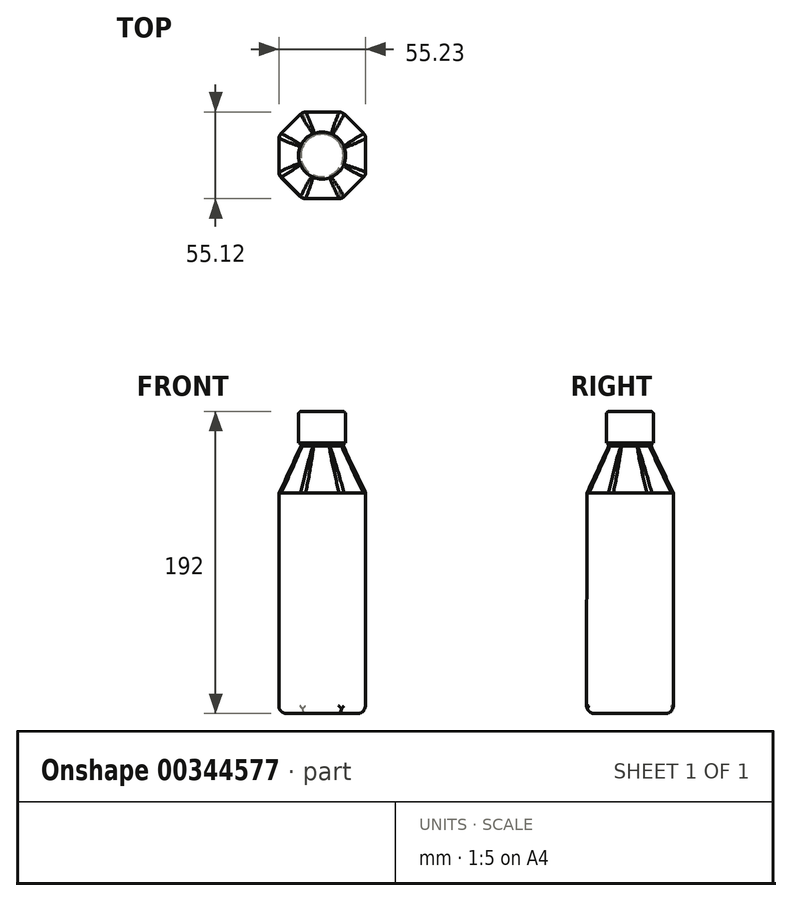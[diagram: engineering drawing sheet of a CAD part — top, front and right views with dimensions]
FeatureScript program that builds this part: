
annotation { "Feature Type Name" : "Feature", "Feature Type Description" : "" }
export const myFeature = defineFeature(function(context is Context, id is Id, definition is map)
    precondition{}
    {
        {
            var Q0;
            Q0=qCreatedBy(makeId("Top.planeOp"),FACE);
            cPlane(context, id + "F0", {"entities" : qUnion([Q0]), "cplaneType" : CPlaneType.OFFSET, "offset" : 140 * mm, "width" : 150 * mm, "height" : 150 * mm});
        }
        {
            var Q0;
            Q0=qCreatedBy(makeId("Top.planeOp"),FACE);
            var sketch = newSketch(context, id + "F1", { "sketchPlane" : qUnion([Q0])});
            skLineSegment(sketch, "E0.bottom", {"start": v(27.5, 27.5) * mm, "end": v(-27.5, 27.5) * mm});
            skLineSegment(sketch, "E0.top", {"start": v(27.5, -27.5) * mm, "end": v(-27.5, -27.5) * mm});
            skLineSegment(sketch, "E0.left", {"start": v(27.5, 27.5) * mm, "end": v(27.5, -27.5) * mm});
            skLineSegment(sketch, "E0.right", {"start": v(-27.5, 27.5) * mm, "end": v(-27.5, -27.5) * mm});
            skPoint(sketch, "E0.middle", {"position": v(0, 0) * mm});
            skSolve(sketch);
        }
        {
            var Q0;
            Q0=qCreatedBy(id+"F0.planeOp",FACE);
            var sketch = newSketch(context, id + "F2", { "sketchPlane" : qUnion([Q0])});
            skLineSegment(sketch, "E1.bottom", {"start": v(27.74, 27.62) * mm, "end": v(-27.26, 27.62) * mm});
            skLineSegment(sketch, "E1.top", {"start": v(27.74, -27.38) * mm, "end": v(-27.26, -27.38) * mm});
            skLineSegment(sketch, "E1.left", {"start": v(27.74, 27.62) * mm, "end": v(27.74, -27.38) * mm});
            skLineSegment(sketch, "E1.right", {"start": v(-27.26, 27.62) * mm, "end": v(-27.26, -27.38) * mm});
            skPoint(sketch, "E1.middle", {"position": v(0.24, 0.12) * mm});
            skSolve(sketch);
        }
        {
            var Q0;
            Q0=makeQuery(id+"F1.imprint","IMPRINT",FACE,{"disambiguationData":[TD([[makeQuery(id+"F1.imprint","IMPRINT",EDGE,{"derivedFrom":sQuery(id+"F1.wireOp",EDGE,"E0.bottom")}),1.0]])]});
            var Q1;
            Q1=makeQuery(id+"F2.imprint","IMPRINT",FACE,{"disambiguationData":[TD([[makeQuery(id+"F2.imprint","IMPRINT",EDGE,{"derivedFrom":sQuery(id+"F2.wireOp",EDGE,"E1.bottom")}),1.0]])]});
            loft(context, id + "F3", {"sheetProfilesArray" : [{ "sheetProfileEntities" : qUnion([Q0]) }, { "sheetProfileEntities" : qUnion([Q1]) }]});
        }
        {
            var Q0;
            Q0=makeQuery(id+"F3.opLoft","SWEPT_EDGE",EDGE,{"disambiguationData":[OSD([sQuery(id+"F1.wireOp",EDGE,"E0.top"),sQuery(id+"F1.wireOp",EDGE,"E0.left"),sQuery(id+"F2.wireOp",EDGE,"E1.top"),sQuery(id+"F2.wireOp",EDGE,"E1.left")])]});
            var Q1;
            Q1=makeQuery(id+"F3.opLoft","SWEPT_EDGE",EDGE,{"disambiguationData":[OSD([sQuery(id+"F1.wireOp",EDGE,"E0.bottom"),sQuery(id+"F1.wireOp",EDGE,"E0.left"),sQuery(id+"F2.wireOp",EDGE,"E1.bottom"),sQuery(id+"F2.wireOp",EDGE,"E1.left")])]});
            var Q2;
            Q2=makeQuery(id+"F3.opLoft","SWEPT_EDGE",EDGE,{"disambiguationData":[OSD([sQuery(id+"F1.wireOp",EDGE,"E0.top"),sQuery(id+"F1.wireOp",EDGE,"E0.right"),sQuery(id+"F2.wireOp",EDGE,"E1.top"),sQuery(id+"F2.wireOp",EDGE,"E1.right")])]});
            var Q3;
            Q3=makeQuery(id+"F3.opLoft","SWEPT_EDGE",EDGE,{"disambiguationData":[OSD([sQuery(id+"F1.wireOp",EDGE,"E0.bottom"),sQuery(id+"F1.wireOp",EDGE,"E0.right"),sQuery(id+"F2.wireOp",EDGE,"E1.bottom"),sQuery(id+"F2.wireOp",EDGE,"E1.right")])]});
            chamfer(context, id + "F4", {"entities" : qUnion([Q0, Q1, Q2, Q3]), "width" : 15 * mm, "tangentPropagation" : true});
        }
        {
            var Q0;
            Q0=qCreatedBy(id+"F0.planeOp",FACE);
            cPlane(context, id + "F5", {"entities" : qUnion([Q0]), "cplaneType" : CPlaneType.OFFSET, "offset" : 30 * mm, "width" : 150 * mm, "height" : 150 * mm});
        }
        {
            var Q0;
            Q0=qCreatedBy(id+"F5.planeOp",FACE);
            var sketch = newSketch(context, id + "F6", { "sketchPlane" : qUnion([Q0])});
            skCircle(sketch, "E2", {"center": v(0, 0) * mm, "radius": 13.5 * mm});
            skSolve(sketch);
        }
        {
            var Q1;
            Q1=makeQuery(id+"F3.opLoft","CAP_FACE",FACE,{"disambiguationData":[OSD([makeQuery(id+"F2.imprint","IMPRINT",FACE,{"disambiguationData":[TD([[makeQuery(id+"F2.imprint","IMPRINT",EDGE,{"derivedFrom":sQuery(id+"F2.wireOp",EDGE,"E1.bottom")}),1.0]])]})])],"isStart":true});
            var Q2;
            Q2=makeQuery(id+"F6.imprint","IMPRINT",FACE,{"disambiguationData":[TD([[makeQuery(id+"F6.imprint","IMPRINT",EDGE,{"derivedFrom":sQuery(id+"F6.wireOp",EDGE,"E2")}),1.0]])]});
            loft(context, id + "F7", {"operationType" : NewBodyOperationType.ADD, "sheetProfilesArray" : [{ "sheetProfileEntities" : qUnion([Q1]) }, { "sheetProfileEntities" : qUnion([Q2]) }]});
        }
        {
            var Q0;
            {var subQ0=sQuery(id+"F1.wireOp",EDGE,"E0.bottom");var subQ1=sQuery(id+"F1.wireOp",EDGE,"E0.left");Q0=makeQuery(id+"F4.opChamfer","BLEND_EDGE",EDGE,{"blendedFrom":[makeQuery(id+"F3.opLoft","SWEPT_EDGE",EDGE,{"disambiguationData":[OSD([subQ0,subQ1,sQuery(id+"F2.wireOp",EDGE,"E1.bottom"),sQuery(id+"F2.wireOp",EDGE,"E1.left")])]}),makeQuery(id+"F3.opLoft","CAP_FACE",FACE,{"disambiguationData":[OSD([makeQuery(id+"F1.imprint","IMPRINT",FACE,{"disambiguationData":[TD([[makeQuery(id+"F1.imprint","IMPRINT",EDGE,{"derivedFrom":subQ0}),1.0]])]})])],"isStart":true})],"blendedInto":[makeQuery(id+"F3.opLoft","CAP_FACE",FACE,{"disambiguationData":[OSD([makeQuery(id+"F1.imprint","IMPRINT",FACE,{"disambiguationData":[TD([[makeQuery(id+"F1.imprint","IMPRINT",EDGE,{"derivedFrom":subQ0}),1.0]])]})])],"isStart":true})]});}
            var Q1;
            Q1=makeQuery(id+"F3.opLoft","MID_CAP_EDGE",EDGE,{"disambiguationData":[OSD([sQuery(id+"F1.wireOp",EDGE,"E0.bottom"),sQuery(id+"F1.wireOp",EDGE,"E0.top"),sQuery(id+"F1.wireOp",EDGE,"E0.left")])],"capPos":0.0});
            var Q2;
            {var subQ0=sQuery(id+"F1.wireOp",EDGE,"E0.top");var subQ1=sQuery(id+"F1.wireOp",EDGE,"E0.left");Q2=makeQuery(id+"F4.opChamfer","BLEND_EDGE",EDGE,{"blendedFrom":[makeQuery(id+"F3.opLoft","SWEPT_EDGE",EDGE,{"disambiguationData":[OSD([subQ0,subQ1,sQuery(id+"F2.wireOp",EDGE,"E1.top"),sQuery(id+"F2.wireOp",EDGE,"E1.left")])]}),makeQuery(id+"F3.opLoft","CAP_FACE",FACE,{"disambiguationData":[OSD([makeQuery(id+"F1.imprint","IMPRINT",FACE,{"disambiguationData":[TD([[makeQuery(id+"F1.imprint","IMPRINT",EDGE,{"derivedFrom":sQuery(id+"F1.wireOp",EDGE,"E0.bottom")}),1.0]])]})])],"isStart":true})],"blendedInto":[makeQuery(id+"F3.opLoft","CAP_FACE",FACE,{"disambiguationData":[OSD([makeQuery(id+"F1.imprint","IMPRINT",FACE,{"disambiguationData":[TD([[makeQuery(id+"F1.imprint","IMPRINT",EDGE,{"derivedFrom":sQuery(id+"F1.wireOp",EDGE,"E0.bottom")}),1.0]])]})])],"isStart":true})]});}
            var Q3;
            Q3=makeQuery(id+"F3.opLoft","MID_CAP_EDGE",EDGE,{"disambiguationData":[OSD([sQuery(id+"F1.wireOp",EDGE,"E0.bottom"),sQuery(id+"F1.wireOp",EDGE,"E0.left"),sQuery(id+"F1.wireOp",EDGE,"E0.right")])],"capPos":0.0});
            var Q4;
            {var subQ0=sQuery(id+"F1.wireOp",EDGE,"E0.bottom");var subQ1=sQuery(id+"F1.wireOp",EDGE,"E0.right");Q4=makeQuery(id+"F4.opChamfer","BLEND_EDGE",EDGE,{"blendedFrom":[makeQuery(id+"F3.opLoft","SWEPT_EDGE",EDGE,{"disambiguationData":[OSD([subQ0,subQ1,sQuery(id+"F2.wireOp",EDGE,"E1.bottom"),sQuery(id+"F2.wireOp",EDGE,"E1.right")])]}),makeQuery(id+"F3.opLoft","CAP_FACE",FACE,{"disambiguationData":[OSD([makeQuery(id+"F1.imprint","IMPRINT",FACE,{"disambiguationData":[TD([[makeQuery(id+"F1.imprint","IMPRINT",EDGE,{"derivedFrom":subQ0}),1.0]])]})])],"isStart":true})],"blendedInto":[makeQuery(id+"F3.opLoft","CAP_FACE",FACE,{"disambiguationData":[OSD([makeQuery(id+"F1.imprint","IMPRINT",FACE,{"disambiguationData":[TD([[makeQuery(id+"F1.imprint","IMPRINT",EDGE,{"derivedFrom":subQ0}),1.0]])]})])],"isStart":true})]});}
            var Q5;
            Q5=makeQuery(id+"F3.opLoft","MID_CAP_EDGE",EDGE,{"disambiguationData":[OSD([sQuery(id+"F1.wireOp",EDGE,"E0.bottom"),sQuery(id+"F1.wireOp",EDGE,"E0.top"),sQuery(id+"F1.wireOp",EDGE,"E0.right")])],"capPos":0.0});
            var Q6;
            {var subQ0=sQuery(id+"F1.wireOp",EDGE,"E0.top");var subQ1=sQuery(id+"F1.wireOp",EDGE,"E0.right");Q6=makeQuery(id+"F4.opChamfer","BLEND_EDGE",EDGE,{"blendedFrom":[makeQuery(id+"F3.opLoft","SWEPT_EDGE",EDGE,{"disambiguationData":[OSD([subQ0,subQ1,sQuery(id+"F2.wireOp",EDGE,"E1.top"),sQuery(id+"F2.wireOp",EDGE,"E1.right")])]}),makeQuery(id+"F3.opLoft","CAP_FACE",FACE,{"disambiguationData":[OSD([makeQuery(id+"F1.imprint","IMPRINT",FACE,{"disambiguationData":[TD([[makeQuery(id+"F1.imprint","IMPRINT",EDGE,{"derivedFrom":sQuery(id+"F1.wireOp",EDGE,"E0.bottom")}),1.0]])]})])],"isStart":true})],"blendedInto":[makeQuery(id+"F3.opLoft","CAP_FACE",FACE,{"disambiguationData":[OSD([makeQuery(id+"F1.imprint","IMPRINT",FACE,{"disambiguationData":[TD([[makeQuery(id+"F1.imprint","IMPRINT",EDGE,{"derivedFrom":sQuery(id+"F1.wireOp",EDGE,"E0.bottom")}),1.0]])]})])],"isStart":true})]});}
            var Q7;
            Q7=makeQuery(id+"F3.opLoft","MID_CAP_EDGE",EDGE,{"disambiguationData":[OSD([sQuery(id+"F1.wireOp",EDGE,"E0.top"),sQuery(id+"F1.wireOp",EDGE,"E0.left"),sQuery(id+"F1.wireOp",EDGE,"E0.right")])],"capPos":0.0});
            fillet(context, id + "F8", {"entities" : qUnion([Q0, Q1, Q2, Q3, Q4, Q5, Q6, Q7]), "radius" : 5 * mm, "tangentPropagation" : true, "allowEdgeOverflow" : false});
        }
        {
            var Q0;
            Q0=qCreatedBy(id+"F5.planeOp",FACE);
            cPlane(context, id + "F9", {"entities" : qUnion([Q0]), "cplaneType" : CPlaneType.OFFSET, "offset" : 2 * mm, "width" : 150 * mm, "height" : 150 * mm});
        }
        {
            var Q0;
            Q0=qCreatedBy(id+"F9.planeOp",FACE);
            var sketch = newSketch(context, id + "F10", { "sketchPlane" : qUnion([Q0])});
            skCircle(sketch, "E3", {"center": v(0, 0) * mm, "radius": 13.5 * mm});
            skSolve(sketch);
        }
        {
            var Q0;
            Q0=makeQuery(id+"F6.imprint","IMPRINT",FACE,{"disambiguationData":[TD([[makeQuery(id+"F6.imprint","IMPRINT",EDGE,{"derivedFrom":sQuery(id+"F6.wireOp",EDGE,"E2")}),1.0]])]});
            var Q1;
            Q1=makeQuery(id+"F10.imprint","IMPRINT",FACE,{"disambiguationData":[TD([[makeQuery(id+"F10.imprint","IMPRINT",EDGE,{"derivedFrom":sQuery(id+"F10.wireOp",EDGE,"E3")}),1.0]])]});
            loft(context, id + "F11", {"sheetProfilesArray" : [{ "sheetProfileEntities" : qUnion([Q0]) }, { "sheetProfileEntities" : qUnion([Q1]) }]});
        }
        {
            var Q0;
            Q0=qCreatedBy(id+"F9.planeOp",FACE);
            var sketch = newSketch(context, id + "F12", { "sketchPlane" : qUnion([Q0])});
            skCircle(sketch, "E4", {"center": v(0, 0) * mm, "radius": 15 * mm});
            skSolve(sketch);
        }
        {
            var Q0;
            Q0=qCreatedBy(id+"F9.planeOp",FACE);
            cPlane(context, id + "F13", {"entities" : qUnion([Q0]), "cplaneType" : CPlaneType.OFFSET, "offset" : 20 * mm, "width" : 150 * mm, "height" : 150 * mm});
        }
        {
            var Q0;
            Q0=qCreatedBy(id+"F13.planeOp",FACE);
            var sketch = newSketch(context, id + "F14", { "sketchPlane" : qUnion([Q0])});
            skCircle(sketch, "E5", {"center": v(0, 0) * mm, "radius": 15 * mm});
            skSolve(sketch);
        }
        {
            var Q1;
            Q1=makeQuery(id+"F14.imprint","IMPRINT",FACE,{"disambiguationData":[TD([[makeQuery(id+"F14.imprint","IMPRINT",EDGE,{"derivedFrom":sQuery(id+"F14.wireOp",EDGE,"E5")}),1.0]])]});
            var Q2;
            Q2=makeQuery(id+"F12.imprint","IMPRINT",FACE,{"disambiguationData":[TD([[makeQuery(id+"F12.imprint","IMPRINT",EDGE,{"derivedFrom":sQuery(id+"F12.wireOp",EDGE,"E4")}),1.0]])]});
            loft(context, id + "F15", {"operationType" : NewBodyOperationType.ADD, "sheetProfilesArray" : [{ "sheetProfileEntities" : qUnion([Q1]) }, { "sheetProfileEntities" : qUnion([Q2]) }]});
        }
        {
            var Q0;
            Q0=makeQuery(id+"F15.opLoft","MID_CAP_EDGE",EDGE,{"disambiguationData":[OSD([sQuery(id+"F14.wireOp",EDGE,"E5")])],"capPos":0.0});
            fillet(context, id + "F16", {"entities" : qUnion([Q0]), "radius" : 2 * mm, "tangentPropagation" : true, "allowEdgeOverflow" : false});
        }
        {
            var Q0;
            {var subQ0=sQuery(id+"F6.wireOp",EDGE,"E2");var subQ1=sQuery(id+"F2.wireOp",EDGE,"E1.bottom");var subQ2=sQuery(id+"F2.wireOp",EDGE,"E1.top");var subQ3=sQuery(id+"F2.wireOp",EDGE,"E1.left");var subQ4=sQuery(id+"F2.wireOp",EDGE,"E1.right");var subQ5=makeQuery(id+"F2.imprint","IMPRINT",FACE,{"disambiguationData":[TD([[makeQuery(id+"F2.imprint","IMPRINT",EDGE,{"derivedFrom":subQ1}),1.0]])]});var subQ6=makeQuery(id+"F3.opLoft","CAP_FACE",FACE,{"disambiguationData":[OSD([subQ5])],"isStart":true});var subQ7=sQuery(id+"F1.wireOp",EDGE,"E0.right");var subQ8=sQuery(id+"F1.wireOp",EDGE,"E0.left");var subQ9=sQuery(id+"F1.wireOp",EDGE,"E0.top");var subQ10=makeQuery(id+"F3.opLoft","SWEPT_EDGE",EDGE,{"disambiguationData":[OSD([subQ9,subQ8,subQ2,subQ3])]});var subQ11=sQuery(id+"F1.wireOp",EDGE,"E0.bottom");Q0=makeQuery(id+"F7.opLoft","SWEPT_EDGE",EDGE,{"disambiguationData":[OSD([subQ11,subQ9,subQ8,subQ7,subQ1,subQ2,subQ3,subQ4,subQ5,subQ0]),TDD([makeQuery(id+"F4.opChamfer","BLEND_VERTEX",VERTEX,{"blendedFrom":[subQ10,makeQuery(id+"F3.opLoft","SWEPT_FACE",FACE,{"disambiguationData":[OSD([subQ11,subQ9,subQ8,subQ1,subQ2,subQ3])]}),subQ6],"blendedInto":[makeQuery(id+"F3.opLoft","SWEPT_FACE",FACE,{"disambiguationData":[OSD([subQ11,subQ9,subQ8,subQ1,subQ2,subQ3])]}),subQ6]}),makeQuery(id+"F4.opChamfer","BLEND_VERTEX",VERTEX,{"blendedFrom":[subQ10,makeQuery(id+"F3.opLoft","SWEPT_FACE",FACE,{"disambiguationData":[OSD([subQ9,subQ8,subQ7,subQ2,subQ3,subQ4])]}),subQ6],"blendedInto":[makeQuery(id+"F3.opLoft","SWEPT_FACE",FACE,{"disambiguationData":[OSD([subQ9,subQ8,subQ7,subQ2,subQ3,subQ4])]}),subQ6]}),makeQuery(id+"F6.imprint","IMPRINT",EDGE,{"derivedFrom":subQ0})])]});}
            var Q1;
            {var subQ0=sQuery(id+"F2.wireOp",EDGE,"E1.bottom");var subQ1=sQuery(id+"F2.wireOp",EDGE,"E1.top");var subQ2=sQuery(id+"F2.wireOp",EDGE,"E1.left");Q1=makeQuery(id+"F7.opLoft","SWEPT_EDGE",EDGE,{"disambiguationData":[OSD([sQuery(id+"F1.wireOp",EDGE,"E0.bottom"),sQuery(id+"F1.wireOp",EDGE,"E0.top"),sQuery(id+"F1.wireOp",EDGE,"E0.left"),subQ0,subQ1,subQ2,makeQuery(id+"F2.imprint","IMPRINT",FACE,{"disambiguationData":[TD([[makeQuery(id+"F2.imprint","IMPRINT",EDGE,{"derivedFrom":subQ0}),1.0]])]}),sQuery(id+"F6.wireOp",EDGE,"E2")])]});}
            var Q2;
            {var subQ0=sQuery(id+"F2.wireOp",EDGE,"E1.bottom");var subQ1=sQuery(id+"F2.wireOp",EDGE,"E1.left");var subQ2=sQuery(id+"F2.wireOp",EDGE,"E1.right");Q2=makeQuery(id+"F7.opLoft","SWEPT_EDGE",EDGE,{"disambiguationData":[OSD([sQuery(id+"F1.wireOp",EDGE,"E0.bottom"),sQuery(id+"F1.wireOp",EDGE,"E0.left"),sQuery(id+"F1.wireOp",EDGE,"E0.right"),subQ0,subQ1,subQ2,makeQuery(id+"F2.imprint","IMPRINT",FACE,{"disambiguationData":[TD([[makeQuery(id+"F2.imprint","IMPRINT",EDGE,{"derivedFrom":subQ0}),1.0]])]})])]});}
            var Q3;
            {var subQ0=sQuery(id+"F2.wireOp",EDGE,"E1.top");var subQ1=sQuery(id+"F2.wireOp",EDGE,"E1.left");var subQ2=sQuery(id+"F2.wireOp",EDGE,"E1.right");Q3=makeQuery(id+"F7.opLoft","SWEPT_EDGE",EDGE,{"disambiguationData":[OSD([sQuery(id+"F1.wireOp",EDGE,"E0.top"),sQuery(id+"F1.wireOp",EDGE,"E0.left"),sQuery(id+"F1.wireOp",EDGE,"E0.right"),subQ0,subQ1,subQ2,makeQuery(id+"F2.imprint","IMPRINT",FACE,{"disambiguationData":[TD([[makeQuery(id+"F2.imprint","IMPRINT",EDGE,{"derivedFrom":sQuery(id+"F2.wireOp",EDGE,"E1.bottom")}),1.0]])]}),sQuery(id+"F6.wireOp",EDGE,"E2")])]});}
            var Q4;
            {var subQ0=sQuery(id+"F2.wireOp",EDGE,"E1.bottom");var subQ1=sQuery(id+"F2.wireOp",EDGE,"E1.top");var subQ2=sQuery(id+"F2.wireOp",EDGE,"E1.right");Q4=makeQuery(id+"F7.opLoft","SWEPT_EDGE",EDGE,{"disambiguationData":[OSD([sQuery(id+"F1.wireOp",EDGE,"E0.bottom"),sQuery(id+"F1.wireOp",EDGE,"E0.top"),sQuery(id+"F1.wireOp",EDGE,"E0.right"),subQ0,subQ1,subQ2,makeQuery(id+"F2.imprint","IMPRINT",FACE,{"disambiguationData":[TD([[makeQuery(id+"F2.imprint","IMPRINT",EDGE,{"derivedFrom":subQ0}),1.0]])]}),sQuery(id+"F6.wireOp",EDGE,"E2")])]});}
            var Q5;
            {var subQ0=sQuery(id+"F6.wireOp",EDGE,"E2");var subQ1=sQuery(id+"F2.wireOp",EDGE,"E1.bottom");var subQ2=sQuery(id+"F2.wireOp",EDGE,"E1.top");var subQ3=sQuery(id+"F2.wireOp",EDGE,"E1.left");var subQ4=sQuery(id+"F2.wireOp",EDGE,"E1.right");var subQ5=makeQuery(id+"F2.imprint","IMPRINT",FACE,{"disambiguationData":[TD([[makeQuery(id+"F2.imprint","IMPRINT",EDGE,{"derivedFrom":subQ1}),1.0]])]});var subQ6=makeQuery(id+"F3.opLoft","CAP_FACE",FACE,{"disambiguationData":[OSD([subQ5])],"isStart":true});var subQ7=sQuery(id+"F1.wireOp",EDGE,"E0.right");var subQ8=sQuery(id+"F1.wireOp",EDGE,"E0.left");var subQ9=sQuery(id+"F1.wireOp",EDGE,"E0.top");var subQ10=makeQuery(id+"F3.opLoft","SWEPT_EDGE",EDGE,{"disambiguationData":[OSD([subQ9,subQ7,subQ2,subQ4])]});var subQ11=sQuery(id+"F1.wireOp",EDGE,"E0.bottom");Q5=makeQuery(id+"F7.opLoft","SWEPT_EDGE",EDGE,{"disambiguationData":[OSD([subQ11,subQ9,subQ8,subQ7,subQ1,subQ2,subQ3,subQ4,subQ5,subQ0]),TDD([makeQuery(id+"F4.opChamfer","BLEND_VERTEX",VERTEX,{"blendedFrom":[subQ10,makeQuery(id+"F3.opLoft","SWEPT_FACE",FACE,{"disambiguationData":[OSD([subQ11,subQ9,subQ7,subQ1,subQ2,subQ4])]}),subQ6],"blendedInto":[makeQuery(id+"F3.opLoft","SWEPT_FACE",FACE,{"disambiguationData":[OSD([subQ11,subQ9,subQ7,subQ1,subQ2,subQ4])]}),subQ6]}),makeQuery(id+"F4.opChamfer","BLEND_VERTEX",VERTEX,{"blendedFrom":[subQ10,makeQuery(id+"F3.opLoft","SWEPT_FACE",FACE,{"disambiguationData":[OSD([subQ9,subQ8,subQ7,subQ2,subQ3,subQ4])]}),subQ6],"blendedInto":[makeQuery(id+"F3.opLoft","SWEPT_FACE",FACE,{"disambiguationData":[OSD([subQ9,subQ8,subQ7,subQ2,subQ3,subQ4])]}),subQ6]}),makeQuery(id+"F6.imprint","IMPRINT",EDGE,{"derivedFrom":subQ0})])]});}
            var Q6;
            {var subQ0=sQuery(id+"F2.wireOp",EDGE,"E1.bottom");var subQ1=sQuery(id+"F2.wireOp",EDGE,"E1.left");var subQ2=sQuery(id+"F2.wireOp",EDGE,"E1.right");Q6=makeQuery(id+"F7.opLoft","SWEPT_EDGE",EDGE,{"disambiguationData":[OSD([sQuery(id+"F1.wireOp",EDGE,"E0.bottom"),sQuery(id+"F1.wireOp",EDGE,"E0.left"),sQuery(id+"F1.wireOp",EDGE,"E0.right"),subQ0,subQ1,subQ2,makeQuery(id+"F2.imprint","IMPRINT",FACE,{"disambiguationData":[TD([[makeQuery(id+"F2.imprint","IMPRINT",EDGE,{"derivedFrom":subQ0}),1.0]])]}),sQuery(id+"F6.wireOp",EDGE,"E2")])]});}
            var Q7;
            {var subQ0=sQuery(id+"F6.wireOp",EDGE,"E2");var subQ1=sQuery(id+"F2.wireOp",EDGE,"E1.bottom");var subQ2=sQuery(id+"F2.wireOp",EDGE,"E1.top");var subQ3=sQuery(id+"F2.wireOp",EDGE,"E1.left");var subQ4=sQuery(id+"F2.wireOp",EDGE,"E1.right");var subQ5=makeQuery(id+"F2.imprint","IMPRINT",FACE,{"disambiguationData":[TD([[makeQuery(id+"F2.imprint","IMPRINT",EDGE,{"derivedFrom":subQ1}),1.0]])]});var subQ6=makeQuery(id+"F3.opLoft","CAP_FACE",FACE,{"disambiguationData":[OSD([subQ5])],"isStart":true});var subQ7=sQuery(id+"F1.wireOp",EDGE,"E0.right");var subQ8=sQuery(id+"F1.wireOp",EDGE,"E0.top");var subQ9=sQuery(id+"F1.wireOp",EDGE,"E0.bottom");var subQ10=makeQuery(id+"F3.opLoft","SWEPT_EDGE",EDGE,{"disambiguationData":[OSD([subQ9,subQ7,subQ1,subQ4])]});var subQ11=sQuery(id+"F1.wireOp",EDGE,"E0.left");Q7=makeQuery(id+"F7.opLoft","SWEPT_EDGE",EDGE,{"disambiguationData":[OSD([subQ9,subQ8,subQ11,subQ7,subQ1,subQ2,subQ3,subQ4,subQ5,subQ0]),TDD([makeQuery(id+"F4.opChamfer","BLEND_VERTEX",VERTEX,{"blendedFrom":[subQ10,makeQuery(id+"F3.opLoft","SWEPT_FACE",FACE,{"disambiguationData":[OSD([subQ9,subQ11,subQ7,subQ1,subQ3,subQ4])]}),subQ6],"blendedInto":[makeQuery(id+"F3.opLoft","SWEPT_FACE",FACE,{"disambiguationData":[OSD([subQ9,subQ11,subQ7,subQ1,subQ3,subQ4])]}),subQ6]}),makeQuery(id+"F4.opChamfer","BLEND_VERTEX",VERTEX,{"blendedFrom":[subQ10,makeQuery(id+"F3.opLoft","SWEPT_FACE",FACE,{"disambiguationData":[OSD([subQ9,subQ8,subQ7,subQ1,subQ2,subQ4])]}),subQ6],"blendedInto":[makeQuery(id+"F3.opLoft","SWEPT_FACE",FACE,{"disambiguationData":[OSD([subQ9,subQ8,subQ7,subQ1,subQ2,subQ4])]}),subQ6]}),makeQuery(id+"F6.imprint","IMPRINT",EDGE,{"derivedFrom":subQ0})])]});}
            fillet(context, id + "F17", {"entities" : qUnion([Q0, Q1, Q2, Q3, Q4, Q5, Q6, Q7]), "radius" : 5 * mm, "tangentPropagation" : true, "allowEdgeOverflow" : false});
        }
        {
            var Q0;
            {var subQ0=sQuery(id+"F2.wireOp",EDGE,"E1.left");var subQ1=sQuery(id+"F2.wireOp",EDGE,"E1.top");var subQ2=sQuery(id+"F1.wireOp",EDGE,"E0.left");var subQ3=sQuery(id+"F1.wireOp",EDGE,"E0.top");Q0=makeQuery(id+"F4.opChamfer","BLEND_EDGE",EDGE,{"blendedFrom":[makeQuery(id+"F3.opLoft","SWEPT_EDGE",EDGE,{"disambiguationData":[OSD([subQ3,subQ2,subQ1,subQ0])]}),makeQuery(id+"F3.opLoft","SWEPT_FACE",FACE,{"disambiguationData":[OSD([subQ3,subQ2,sQuery(id+"F1.wireOp",EDGE,"E0.right"),subQ1,subQ0,sQuery(id+"F2.wireOp",EDGE,"E1.right")])]})],"blendedInto":[makeQuery(id+"F3.opLoft","SWEPT_FACE",FACE,{"disambiguationData":[OSD([subQ3,subQ2,sQuery(id+"F1.wireOp",EDGE,"E0.right"),subQ1,subQ0,sQuery(id+"F2.wireOp",EDGE,"E1.right")])]})]});}
            var Q1;
            {var subQ0=sQuery(id+"F2.wireOp",EDGE,"E1.left");var subQ1=sQuery(id+"F2.wireOp",EDGE,"E1.top");var subQ2=sQuery(id+"F1.wireOp",EDGE,"E0.left");var subQ3=sQuery(id+"F1.wireOp",EDGE,"E0.top");Q1=makeQuery(id+"F4.opChamfer","BLEND_EDGE",EDGE,{"blendedFrom":[makeQuery(id+"F3.opLoft","SWEPT_EDGE",EDGE,{"disambiguationData":[OSD([subQ3,subQ2,subQ1,subQ0])]}),makeQuery(id+"F3.opLoft","SWEPT_FACE",FACE,{"disambiguationData":[OSD([sQuery(id+"F1.wireOp",EDGE,"E0.bottom"),subQ3,subQ2,sQuery(id+"F2.wireOp",EDGE,"E1.bottom"),subQ1,subQ0])]})],"blendedInto":[makeQuery(id+"F3.opLoft","SWEPT_FACE",FACE,{"disambiguationData":[OSD([sQuery(id+"F1.wireOp",EDGE,"E0.bottom"),subQ3,subQ2,sQuery(id+"F2.wireOp",EDGE,"E1.bottom"),subQ1,subQ0])]})]});}
            var Q2;
            {var subQ0=sQuery(id+"F2.wireOp",EDGE,"E1.left");var subQ1=sQuery(id+"F2.wireOp",EDGE,"E1.bottom");var subQ2=sQuery(id+"F1.wireOp",EDGE,"E0.left");var subQ3=sQuery(id+"F1.wireOp",EDGE,"E0.bottom");Q2=makeQuery(id+"F4.opChamfer","BLEND_EDGE",EDGE,{"blendedFrom":[makeQuery(id+"F3.opLoft","SWEPT_EDGE",EDGE,{"disambiguationData":[OSD([subQ3,subQ2,subQ1,subQ0])]}),makeQuery(id+"F3.opLoft","SWEPT_FACE",FACE,{"disambiguationData":[OSD([subQ3,sQuery(id+"F1.wireOp",EDGE,"E0.top"),subQ2,subQ1,sQuery(id+"F2.wireOp",EDGE,"E1.top"),subQ0])]})],"blendedInto":[makeQuery(id+"F3.opLoft","SWEPT_FACE",FACE,{"disambiguationData":[OSD([subQ3,sQuery(id+"F1.wireOp",EDGE,"E0.top"),subQ2,subQ1,sQuery(id+"F2.wireOp",EDGE,"E1.top"),subQ0])]})]});}
            var Q3;
            {var subQ0=sQuery(id+"F2.wireOp",EDGE,"E1.left");var subQ1=sQuery(id+"F2.wireOp",EDGE,"E1.bottom");var subQ2=sQuery(id+"F1.wireOp",EDGE,"E0.left");var subQ3=sQuery(id+"F1.wireOp",EDGE,"E0.bottom");Q3=makeQuery(id+"F4.opChamfer","BLEND_EDGE",EDGE,{"blendedFrom":[makeQuery(id+"F3.opLoft","SWEPT_EDGE",EDGE,{"disambiguationData":[OSD([subQ3,subQ2,subQ1,subQ0])]}),makeQuery(id+"F3.opLoft","SWEPT_FACE",FACE,{"disambiguationData":[OSD([subQ3,subQ2,sQuery(id+"F1.wireOp",EDGE,"E0.right"),subQ1,subQ0,sQuery(id+"F2.wireOp",EDGE,"E1.right")])]})],"blendedInto":[makeQuery(id+"F3.opLoft","SWEPT_FACE",FACE,{"disambiguationData":[OSD([subQ3,subQ2,sQuery(id+"F1.wireOp",EDGE,"E0.right"),subQ1,subQ0,sQuery(id+"F2.wireOp",EDGE,"E1.right")])]})]});}
            var Q4;
            {var subQ0=sQuery(id+"F2.wireOp",EDGE,"E1.right");var subQ1=sQuery(id+"F2.wireOp",EDGE,"E1.top");var subQ2=sQuery(id+"F1.wireOp",EDGE,"E0.right");var subQ3=sQuery(id+"F1.wireOp",EDGE,"E0.top");Q4=makeQuery(id+"F4.opChamfer","BLEND_EDGE",EDGE,{"blendedFrom":[makeQuery(id+"F3.opLoft","SWEPT_EDGE",EDGE,{"disambiguationData":[OSD([subQ3,subQ2,subQ1,subQ0])]}),makeQuery(id+"F3.opLoft","SWEPT_FACE",FACE,{"disambiguationData":[OSD([sQuery(id+"F1.wireOp",EDGE,"E0.bottom"),subQ3,subQ2,sQuery(id+"F2.wireOp",EDGE,"E1.bottom"),subQ1,subQ0])]})],"blendedInto":[makeQuery(id+"F3.opLoft","SWEPT_FACE",FACE,{"disambiguationData":[OSD([sQuery(id+"F1.wireOp",EDGE,"E0.bottom"),subQ3,subQ2,sQuery(id+"F2.wireOp",EDGE,"E1.bottom"),subQ1,subQ0])]})]});}
            var Q5;
            {var subQ0=sQuery(id+"F2.wireOp",EDGE,"E1.right");var subQ1=sQuery(id+"F2.wireOp",EDGE,"E1.top");var subQ2=sQuery(id+"F1.wireOp",EDGE,"E0.right");var subQ3=sQuery(id+"F1.wireOp",EDGE,"E0.top");Q5=makeQuery(id+"F4.opChamfer","BLEND_EDGE",EDGE,{"blendedFrom":[makeQuery(id+"F3.opLoft","SWEPT_EDGE",EDGE,{"disambiguationData":[OSD([subQ3,subQ2,subQ1,subQ0])]}),makeQuery(id+"F3.opLoft","SWEPT_FACE",FACE,{"disambiguationData":[OSD([subQ3,sQuery(id+"F1.wireOp",EDGE,"E0.left"),subQ2,subQ1,sQuery(id+"F2.wireOp",EDGE,"E1.left"),subQ0])]})],"blendedInto":[makeQuery(id+"F3.opLoft","SWEPT_FACE",FACE,{"disambiguationData":[OSD([subQ3,sQuery(id+"F1.wireOp",EDGE,"E0.left"),subQ2,subQ1,sQuery(id+"F2.wireOp",EDGE,"E1.left"),subQ0])]})]});}
            var Q6;
            {var subQ0=sQuery(id+"F2.wireOp",EDGE,"E1.right");var subQ1=sQuery(id+"F2.wireOp",EDGE,"E1.bottom");var subQ2=sQuery(id+"F1.wireOp",EDGE,"E0.right");var subQ3=sQuery(id+"F1.wireOp",EDGE,"E0.bottom");Q6=makeQuery(id+"F4.opChamfer","BLEND_EDGE",EDGE,{"blendedFrom":[makeQuery(id+"F3.opLoft","SWEPT_EDGE",EDGE,{"disambiguationData":[OSD([subQ3,subQ2,subQ1,subQ0])]}),makeQuery(id+"F3.opLoft","SWEPT_FACE",FACE,{"disambiguationData":[OSD([subQ3,sQuery(id+"F1.wireOp",EDGE,"E0.top"),subQ2,subQ1,sQuery(id+"F2.wireOp",EDGE,"E1.top"),subQ0])]})],"blendedInto":[makeQuery(id+"F3.opLoft","SWEPT_FACE",FACE,{"disambiguationData":[OSD([subQ3,sQuery(id+"F1.wireOp",EDGE,"E0.top"),subQ2,subQ1,sQuery(id+"F2.wireOp",EDGE,"E1.top"),subQ0])]})]});}
            var Q7;
            {var subQ0=sQuery(id+"F2.wireOp",EDGE,"E1.right");var subQ1=sQuery(id+"F2.wireOp",EDGE,"E1.bottom");var subQ2=sQuery(id+"F1.wireOp",EDGE,"E0.right");var subQ3=sQuery(id+"F1.wireOp",EDGE,"E0.bottom");Q7=makeQuery(id+"F4.opChamfer","BLEND_EDGE",EDGE,{"blendedFrom":[makeQuery(id+"F3.opLoft","SWEPT_EDGE",EDGE,{"disambiguationData":[OSD([subQ3,subQ2,subQ1,subQ0])]}),makeQuery(id+"F3.opLoft","SWEPT_FACE",FACE,{"disambiguationData":[OSD([subQ3,sQuery(id+"F1.wireOp",EDGE,"E0.left"),subQ2,subQ1,sQuery(id+"F2.wireOp",EDGE,"E1.left"),subQ0])]})],"blendedInto":[makeQuery(id+"F3.opLoft","SWEPT_FACE",FACE,{"disambiguationData":[OSD([subQ3,sQuery(id+"F1.wireOp",EDGE,"E0.left"),subQ2,subQ1,sQuery(id+"F2.wireOp",EDGE,"E1.left"),subQ0])]})]});}
            fillet(context, id + "F18", {"entities" : qUnion([Q0, Q1, Q2, Q3, Q4, Q5, Q6, Q7]), "radius" : 5 * mm, "tangentPropagation" : true, "allowEdgeOverflow" : false});
        }
        {
            var Q0;
            Q0=qCreatedBy(id+"F13.planeOp",FACE);
            cPlane(context, id + "F19", {"entities" : qUnion([Q0]), "cplaneType" : CPlaneType.OFFSET, "offset" : 37 * mm, "width" : 150 * mm, "height" : 150 * mm});
        }
    });
